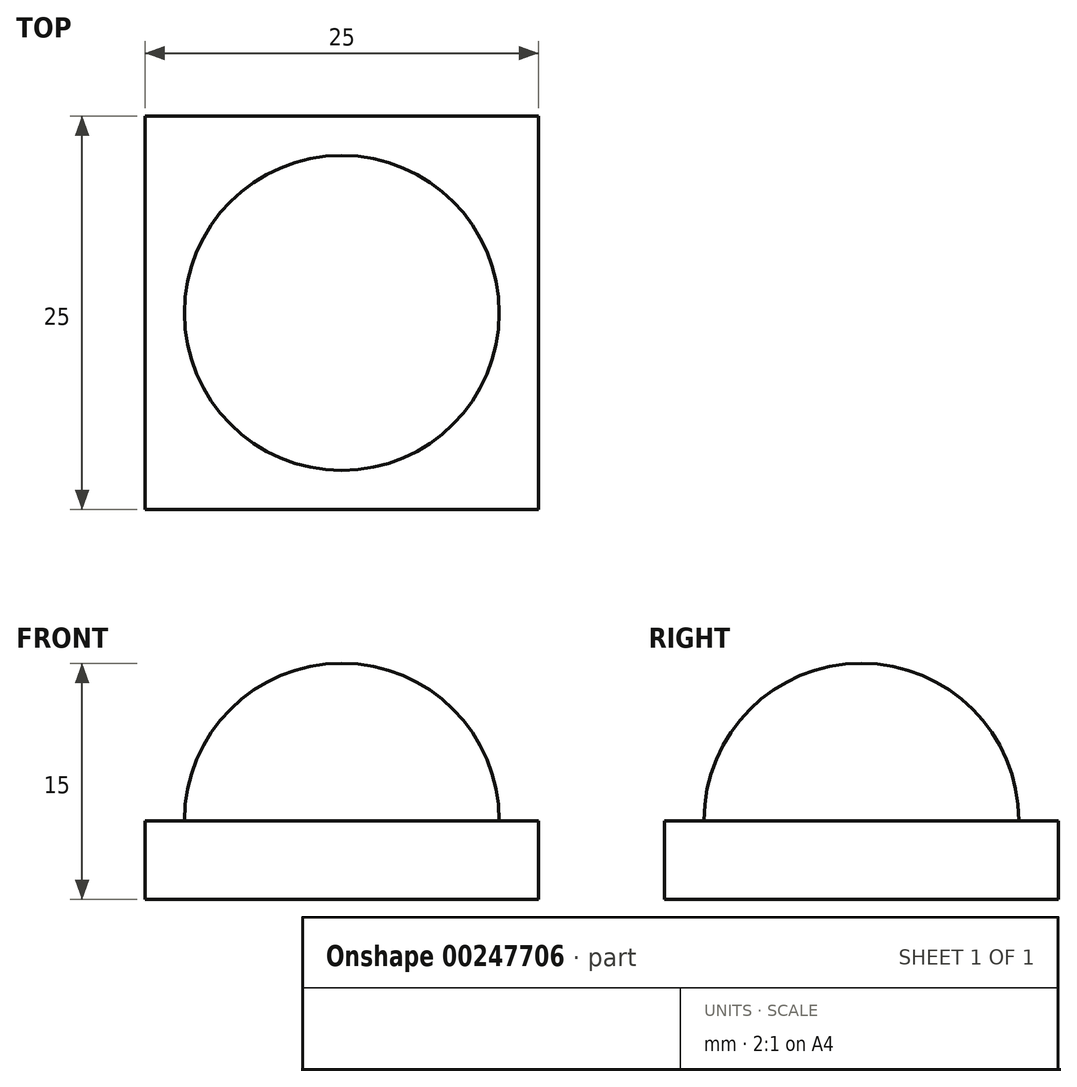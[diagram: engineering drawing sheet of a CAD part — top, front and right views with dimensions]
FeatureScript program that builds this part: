
annotation { "Feature Type Name" : "Feature", "Feature Type Description" : "" }
export const myFeature = defineFeature(function(context is Context, id is Id, definition is map)
    precondition{}
    {
        {
            var Q0;
            Q0=qCreatedBy(makeId("Top.planeOp"),FACE);
            var sketch = newSketch(context, id + "F0", { "sketchPlane" : qUnion([Q0])});
            skLineSegment(sketch, "E0.bottom", {"start": v(12.5, -12.5) * mm, "end": v(-12.5, -12.5) * mm});
            skLineSegment(sketch, "E0.top", {"start": v(12.5, 12.5) * mm, "end": v(-12.5, 12.5) * mm});
            skLineSegment(sketch, "E0.left", {"start": v(12.5, -12.5) * mm, "end": v(12.5, 12.5) * mm});
            skLineSegment(sketch, "E0.right", {"start": v(-12.5, -12.5) * mm, "end": v(-12.5, 12.5) * mm});
            skPoint(sketch, "E0.middle", {"position": v(0, 0) * mm});
            skSolve(sketch);
        }
        {
            var Q0;
            Q0 = qSketchRegion(id + "F0", true);
            extrude(context, id + "F1", {"entities" : qUnion([Q0]), "depth" : 5 * mm});
        }
        {
            var Q0;
            Q0=makeQuery(id+"F1.opExtrude","CAP_FACE",FACE,{"disambiguationData":[OSD([sQuery(id+"F0.wireOp",EDGE,"E0.bottom"),sQuery(id+"F0.wireOp",EDGE,"E0.top"),sQuery(id+"F0.wireOp",EDGE,"E0.left"),sQuery(id+"F0.wireOp",EDGE,"E0.right")])],"isStart":false});
            var sketch = newSketch(context, id + "F2", { "sketchPlane" : qUnion([Q0])});
            skCircle(sketch, "E1", {"center": v(0, 0) * mm, "radius": 10 * mm});
            skLineSegment(sketch, "E2", {"start": v(0, -10) * mm, "end": v(0, 10) * mm});
            skSolve(sketch);
        }
        {
            var Q0;
            {var subQ0=sQuery(id+"F2.wireOp",EDGE,"E2");Q0=makeQuery(id+"F2.imprint","IMPRINT",FACE,{"disambiguationData":[TD([[makeQuery(id+"F2.imprint","IMPRINT",EDGE,{"derivedFrom":subQ0}),1.0]])]});}
            var Q1;
            Q1=sQuery(id+"F2.wireOp",EDGE,"E2");
            revolve(context, id + "F3", {"operationType" : NewBodyOperationType.ADD, "entities" : qUnion([Q0]), "axis" : qUnion([Q1]), "revolveType" : RevolveType.ONE_DIRECTION, "angle" : 180 * degree});
        }
    });
